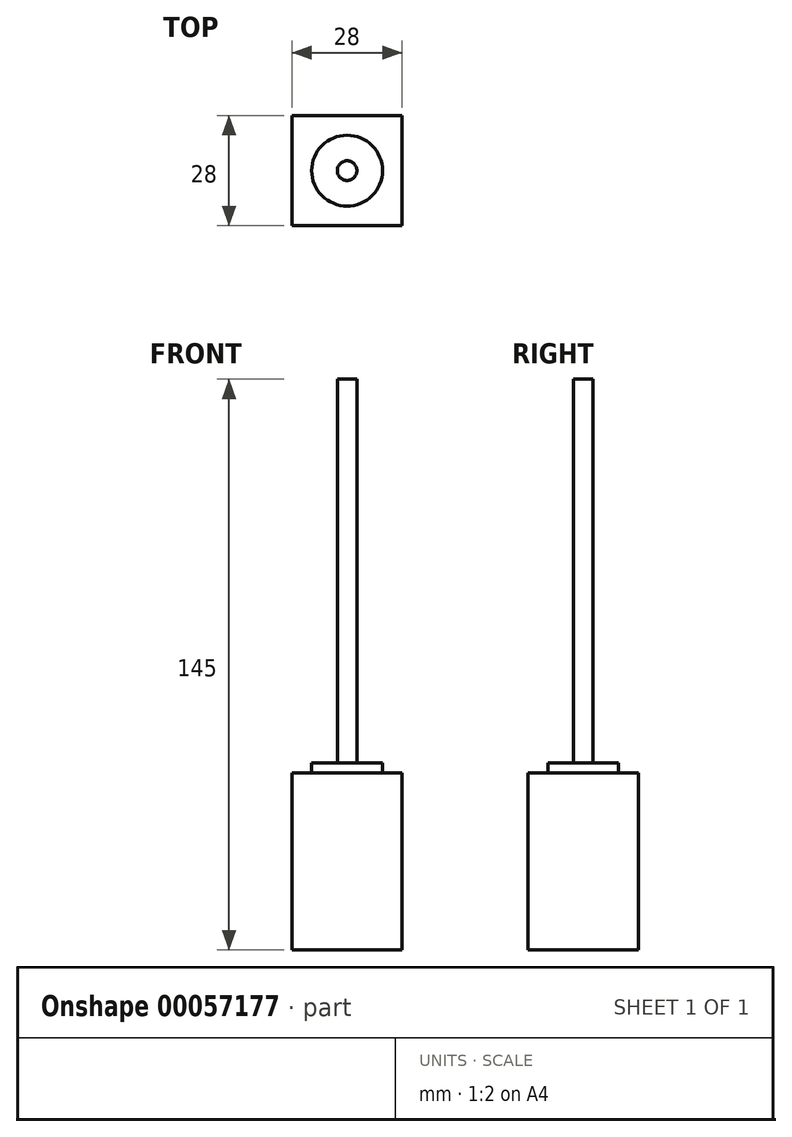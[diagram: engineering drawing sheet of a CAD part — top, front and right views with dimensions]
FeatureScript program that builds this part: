
annotation { "Feature Type Name" : "Feature", "Feature Type Description" : "" }
export const myFeature = defineFeature(function(context is Context, id is Id, definition is map)
    precondition{}
    {
        {
            var Q0;
            Q0=qCreatedBy(makeId("Top.planeOp"),FACE);
            var sketch = newSketch(context, id + "F0", { "sketchPlane" : qUnion([Q0])});
            skLineSegment(sketch, "E0.rect.bottom", {"start": v(14, 14) * mm, "end": v(-14, 14) * mm});
            skLineSegment(sketch, "E0.rect.top", {"start": v(14, -14) * mm, "end": v(-14, -14) * mm});
            skLineSegment(sketch, "E0.rect.left", {"start": v(14, 14) * mm, "end": v(14, -14) * mm});
            skLineSegment(sketch, "E0.rect.right", {"start": v(-14, 14) * mm, "end": v(-14, -14) * mm});
            skPoint(sketch, "E0.rect.middle", {"position": v(0, 0) * mm});
            skCircle(sketch, "E1", {"center": v(0, 0) * mm, "radius": 2.5 * mm});
            skCircle(sketch, "E2", {"center": v(0, 0) * mm, "radius": 9 * mm});
            skSolve(sketch);
        }
        {
            var Q0;
            Q0=makeQuery(id+"F0.imprint","IMPRINT",FACE,{"disambiguationData":[TD([[makeQuery(id+"F0.imprint","IMPRINT",EDGE,{"derivedFrom":sQuery(id+"F0.wireOp",EDGE,"E0.rect.bottom")}),1.0]])]});
            var Q1;
            Q1=makeQuery(id+"F0.imprint","IMPRINT",FACE,{"disambiguationData":[TD([[makeQuery(id+"F0.imprint","IMPRINT",EDGE,{"derivedFrom":sQuery(id+"F0.wireOp",EDGE,"E1")}),-1.0]])]});
            var Q2;
            Q2=makeQuery(id+"F0.imprint","IMPRINT",FACE,{"disambiguationData":[TD([[makeQuery(id+"F0.imprint","IMPRINT",EDGE,{"derivedFrom":sQuery(id+"F0.wireOp",EDGE,"E1")}),1.0]])]});
            extrude(context, id + "F1", {"entities" : qUnion([Q0, Q1, Q2]), "oppositeDirection" : true, "depth" : 45 * mm});
        }
        {
            var Q0;
            Q0=makeQuery(id+"F0.imprint","IMPRINT",FACE,{"disambiguationData":[TD([[makeQuery(id+"F0.imprint","IMPRINT",EDGE,{"derivedFrom":sQuery(id+"F0.wireOp",EDGE,"E1")}),1.0]])]});
            extrude(context, id + "F2", {"entities" : qUnion([Q0]), "operationType" : NewBodyOperationType.ADD, "depth" : 100 * mm});
        }
        {
            var Q0;
            Q0=makeQuery(id+"F0.imprint","IMPRINT",FACE,{"disambiguationData":[TD([[makeQuery(id+"F0.imprint","IMPRINT",EDGE,{"derivedFrom":sQuery(id+"F0.wireOp",EDGE,"E1")}),-1.0]])]});
            extrude(context, id + "F3", {"entities" : qUnion([Q0]), "operationType" : NewBodyOperationType.ADD, "depth" : 2.54 * mm});
        }
    });
